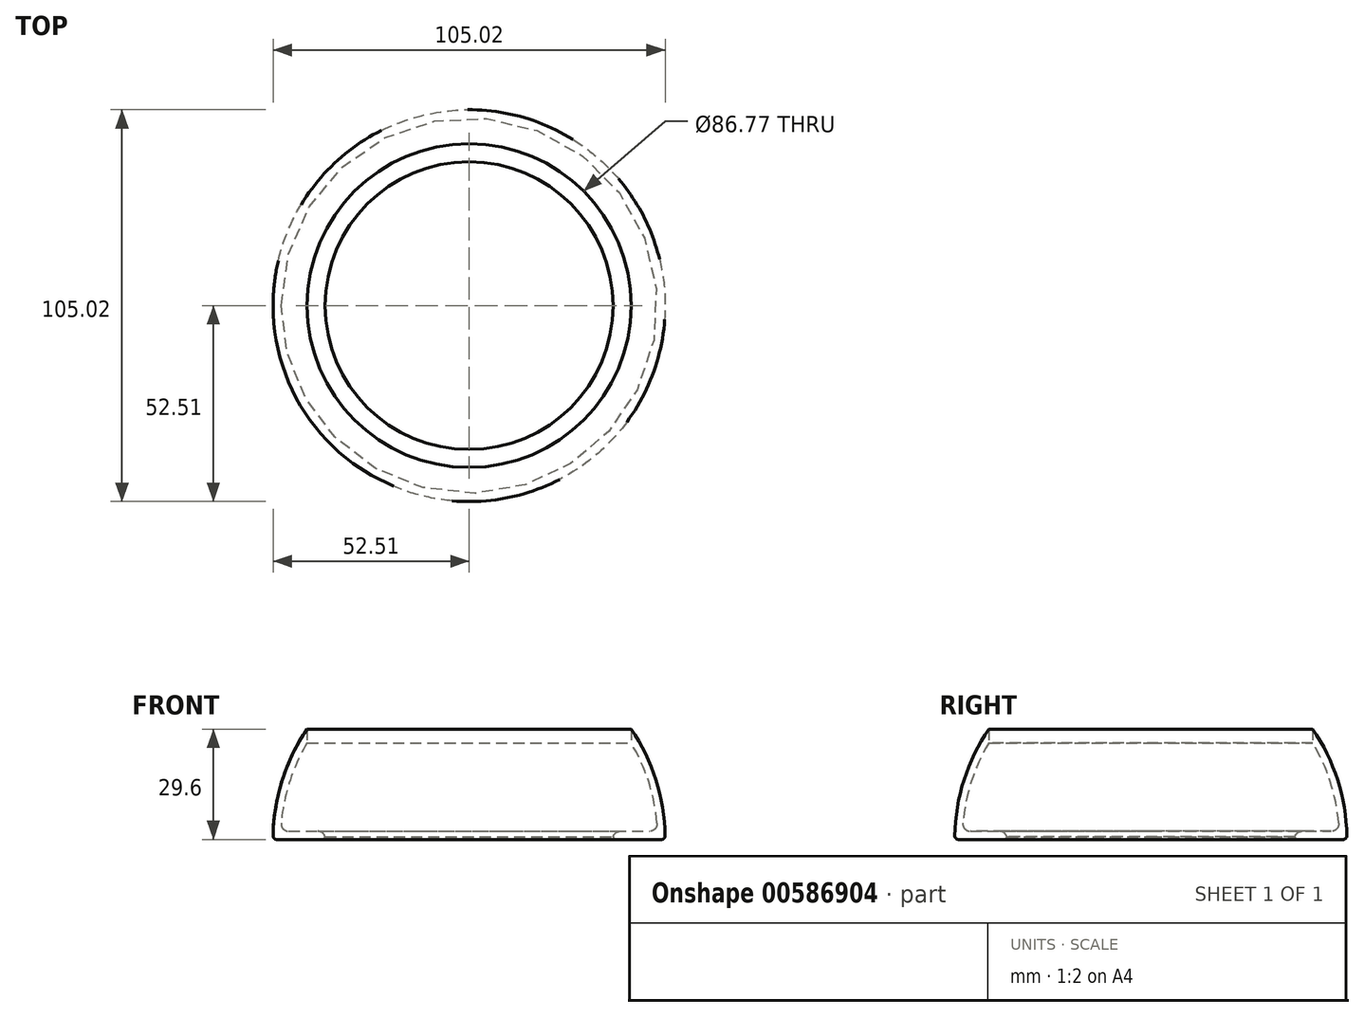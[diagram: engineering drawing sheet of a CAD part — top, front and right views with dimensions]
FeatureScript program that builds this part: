
annotation { "Feature Type Name" : "Feature", "Feature Type Description" : "" }
export const myFeature = defineFeature(function(context is Context, id is Id, definition is map)
    precondition{}
    {
        {
            var Q0;
            Q0=qCreatedBy(makeId("Front.planeOp"),FACE);
            var sketch = newSketch(context, id + "F0", { "sketchPlane" : qUnion([Q0])});
            skArc(sketch, "E0", {"start": v(-43.38, 29.6) * mm, "mid": v(-50.03, 15.97) * mm, "end": v(-52.5, 1.02) * mm});
            skLineSegment(sketch, "E1", {"start": v(-51.5, 0) * mm, "end": v(-39.5, 0) * mm});
            skLineSegment(sketch, "E2", {"start": v(-38.5, 1) * mm, "end": v(-38.5, 0.2) * mm});
            skPoint(sketch, "E3.end.orphan", {"position": v(0, 52.52) * mm});
            skPoint(sketch, "E4.visualSharp", {"position": v(-38.5, 1.2) * mm});
            skLineSegment(sketch, "E4.filletArc", {"start": v(-38.5, 2.2) * mm, "end": v(-38.5, 2.2) * mm});
            skArc(sketch, "E5", {"start": v(-43.38, 25.88) * mm, "mid": v(-48.07, 15.52) * mm, "end": v(-50.33, 4.37) * mm});
            skLineSegment(sketch, "E6", {"start": v(-48.34, 2.2) * mm, "end": v(-40.5, 2.2) * mm});
            skPoint(sketch, "E7.visualSharp", {"position": v(-50.47, 2.2) * mm});
            skArc(sketch, "E7.filletArc", {"start": v(-50.33, 4.37) * mm, "mid": v(-49.81, 2.85) * mm, "end": v(-48.34, 2.2) * mm});
            skPoint(sketch, "E8.visualSharp", {"position": v(-38.5, 0) * mm});
            skArc(sketch, "E8.filletArc", {"start": v(-39.5, 0) * mm, "mid": v(-38.8, 0.3) * mm, "end": v(-38.5, 1) * mm});
            skPoint(sketch, "E9.visualSharp", {"position": v(-38.5, 2.2) * mm});
            skArc(sketch, "E9.filletArc", {"start": v(-38.5, 0.2) * mm, "mid": v(-39.1, 1.61) * mm, "end": v(-40.5, 2.2) * mm});
            skPoint(sketch, "E10.visualSharp", {"position": v(-52.52, 0) * mm});
            skArc(sketch, "E10.filletArc", {"start": v(-52.5, 1.02) * mm, "mid": v(-52.22, 0.3) * mm, "end": v(-51.5, 0) * mm});
            skPoint(sketch, "E11", {"position": v(-43.38, 25.88) * mm});
            skPoint(sketch, "E11.positionSnap0", {"position": v(-43.38, 29.6) * mm});
            skLineSegment(sketch, "E12", {"start": v(-43.38, 29.6) * mm, "end": v(-43.38, 25.88) * mm});
            skLineSegment(sketch, "E13", {"start": v(0, 0) * mm, "end": v(0, 65.73) * mm, "construction": true});
            skSolve(sketch);
        }
        {
            var Q0;
            Q0=makeQuery(id+"F0.imprint","IMPRINT",FACE,{"disambiguationData":[TD([[makeQuery(id+"F0.imprint","IMPRINT",EDGE,{"derivedFrom":sQuery(id+"F0.wireOp",EDGE,"E0")}),1.0]])]});
            var Q1;
            Q1=sQuery(id+"F0.wireOp",EDGE,"E13");
            revolve(context, id + "F1", {"entities" : qUnion([Q0]), "axis" : qUnion([Q1]), "revolveType" : RevolveType.FULL});
        }
    });
